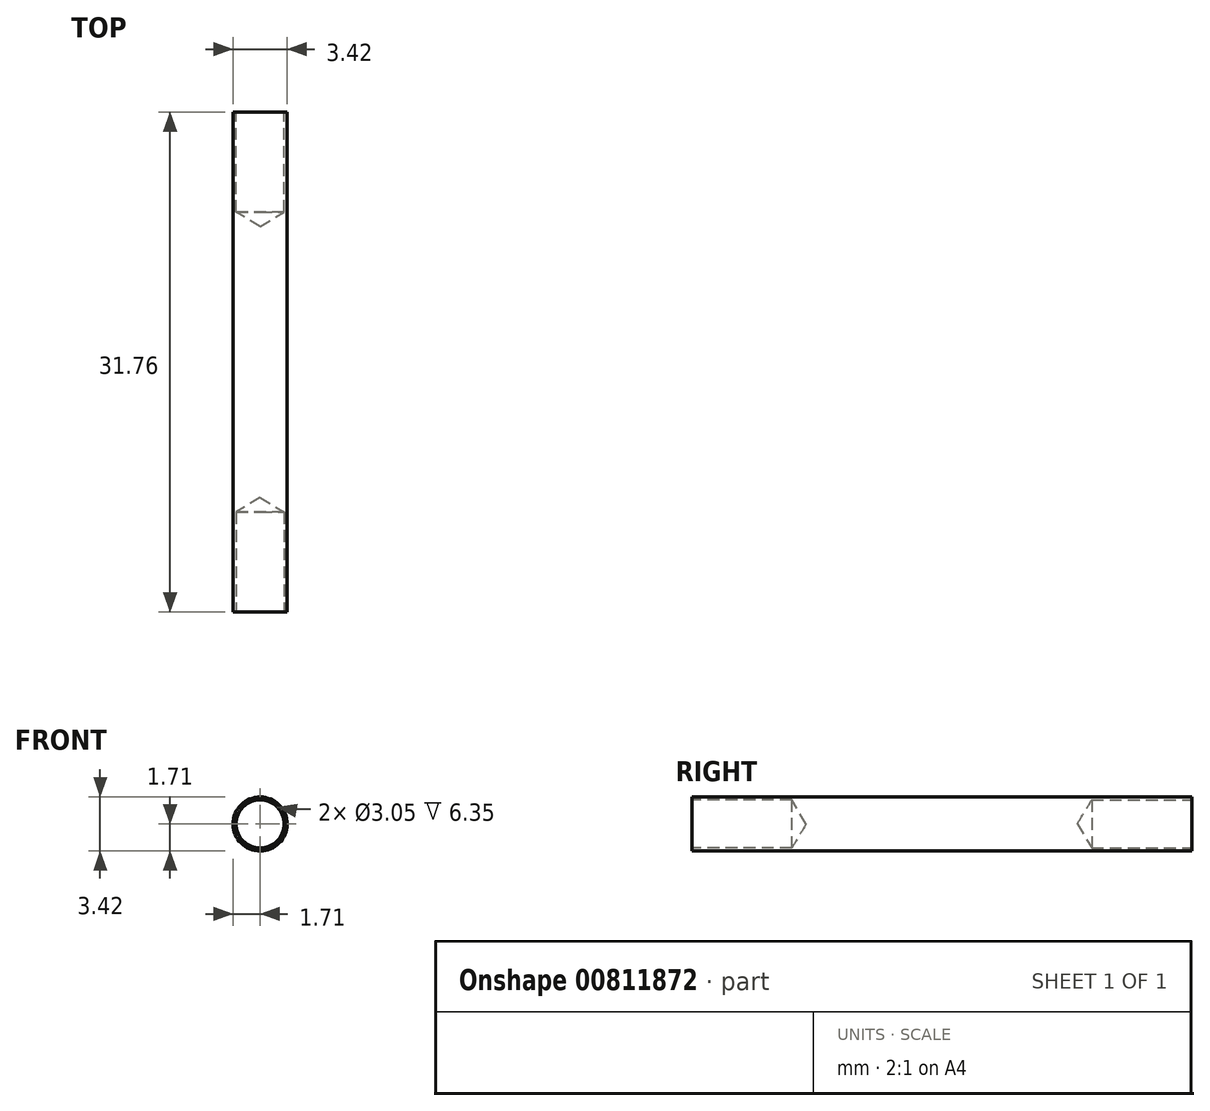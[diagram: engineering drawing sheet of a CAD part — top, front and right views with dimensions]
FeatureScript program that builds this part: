
annotation { "Feature Type Name" : "Feature", "Feature Type Description" : "" }
export const myFeature = defineFeature(function(context is Context, id is Id, definition is map)
    precondition{}
    {
        {
            var Q0;
            Q0=qCreatedBy(makeId("Front.planeOp"),FACE);
            var sketch = newSketch(context, id + "F0", { "sketchPlane" : qUnion([Q0])});
            skCircle(sketch, "E0", {"center": v(0, 0) * mm, "radius": 1.71 * mm});
            skSolve(sketch);
        }
        {
            var Q0;
            Q0 = qSketchRegion(id + "F0", true);
            extrude(context, id + "F1", {"entities" : qUnion([Q0]), "endBound" : BoundingType.SYMMETRIC, "depth" : 31.75 * mm, "offsetDistance" : 25.4 * mm});
        }
        {
            var Q0;
            Q0=makeQuery(id+"F1.opExtrude","CAP_FACE",FACE,{"disambiguationData":[OSD([sQuery(id+"F0.wireOp",EDGE,"E0")])],"isStart":false});
            var sketch = newSketch(context, id + "F2", { "sketchPlane" : qUnion([Q0])});
            skCircle(sketch, "E1", {"center": v(0, 0) * mm, "radius": 1.52 * mm});
            skSolve(sketch);
        }
        {
            var Q0;
            Q0=sQuery(id+"F2.wireOp",VERTEX,"E1.center");
            var Q1;
            Q1=makeQuery(id+"F1.opExtrude","SWEPT_BODY",BODY,{"disambiguationData":[OSD([sQuery(id+"F0.wireOp",EDGE,"E0")])]});
            hole(context, id + "F3", {"style" : HoleStyle.SIMPLE, "endStyle" : HoleEndStyle.BLIND, "holeDiameter" : 3.05 * mm, "majorDiameter" : 6.35 * mm, "holeDepth" : 6.35 * mm, "isTappedThrough" : true, "tappedDepth" : 12.7 * mm, "tapClearance" : 3, "locations" : qUnion([Q0]), "scope" : qUnion([Q1])});
        }
        {
            var Q0;
            Q0=makeQuery(id+"F1.opExtrude","CAP_FACE",FACE,{"disambiguationData":[OSD([sQuery(id+"F0.wireOp",EDGE,"E0")])],"isStart":true});
            var sketch = newSketch(context, id + "F4", { "sketchPlane" : qUnion([Q0])});
            skCircle(sketch, "E2", {"center": v(0, 0) * mm, "radius": 1.52 * mm});
            skSolve(sketch);
        }
        {
            var Q0;
            Q0=sQuery(id+"F4.wireOp",VERTEX,"E2.center");
            var Q1;
            Q1=makeQuery(id+"F1.opExtrude","SWEPT_BODY",BODY,{"disambiguationData":[OSD([sQuery(id+"F0.wireOp",EDGE,"E0")])]});
            hole(context, id + "F5", {"style" : HoleStyle.SIMPLE, "endStyle" : HoleEndStyle.BLIND, "holeDiameter" : 3.05 * mm, "majorDiameter" : 6.35 * mm, "holeDepth" : 6.35 * mm, "isTappedThrough" : true, "tappedDepth" : 12.7 * mm, "tapClearance" : 3, "locations" : qUnion([Q0]), "scope" : qUnion([Q1])});
        }
    });
